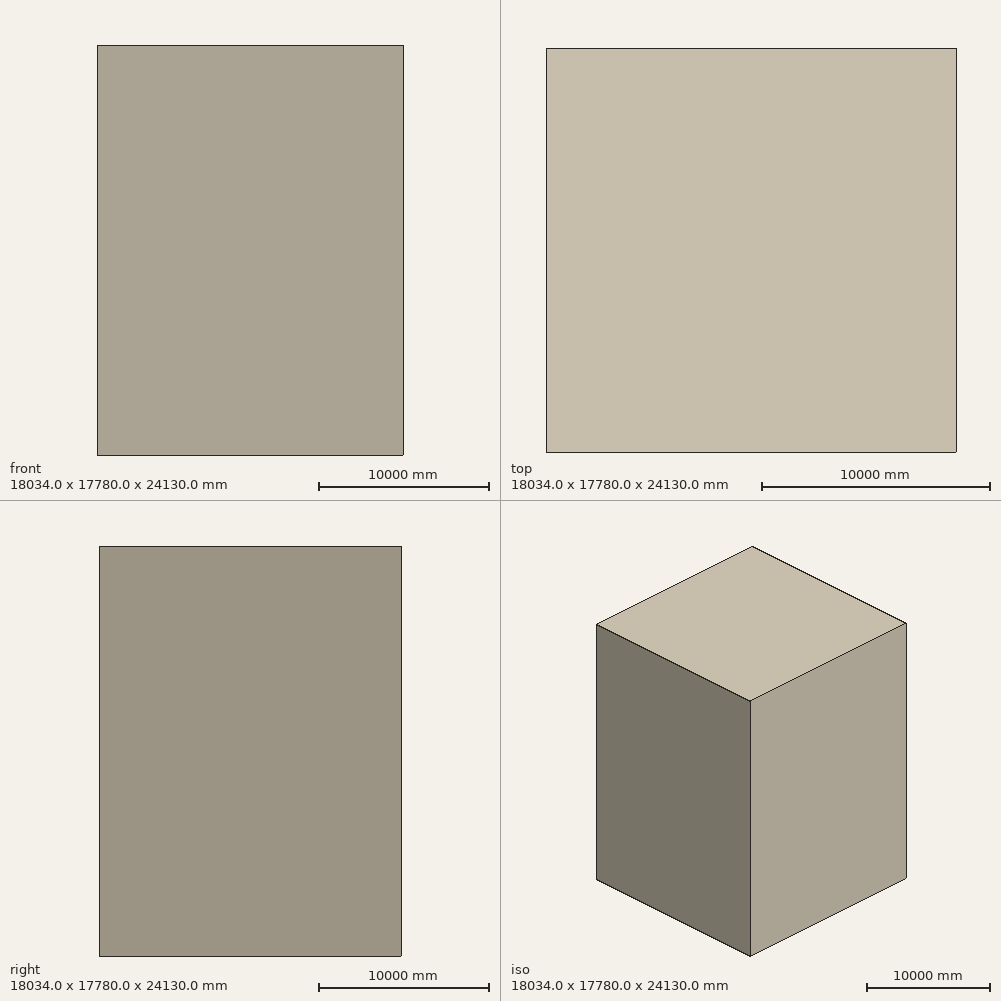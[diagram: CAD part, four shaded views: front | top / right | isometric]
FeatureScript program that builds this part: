
annotation { "Feature Type Name" : "Feature", "Feature Type Description" : "" }
export const myFeature = defineFeature(function(context is Context, id is Id, definition is map)
    precondition{}
    {
        {
            var Q0;
            Q0=qCreatedBy(makeId("Front.planeOp"),FACE);
            var sketch = newSketch(context, id + "F0", { "sketchPlane" : qUnion([Q0])});
            skLineSegment(sketch, "E0.bottom", {"start": v(0, 0) * mm, "end": v(18034, 0) * mm});
            skLineSegment(sketch, "E0.top", {"start": v(0, 24130) * mm, "end": v(18034, 24130) * mm});
            skLineSegment(sketch, "E0.left", {"start": v(0, 0) * mm, "end": v(0, 24130) * mm});
            skLineSegment(sketch, "E0.right", {"start": v(18034, 0) * mm, "end": v(18034, 24130) * mm});
            skSolve(sketch);
        }
        {
            var Q0;
            Q0=makeQuery(id+"F0.imprint","IMPRINT",FACE,{"disambiguationData":[TD([[makeQuery(id+"F0.imprint","IMPRINT",EDGE,{"derivedFrom":sQuery(id+"F0.wireOp",EDGE,"E0.bottom")}),1.0]])]});
            extrude(context, id + "F1", {"entities" : qUnion([Q0]), "oppositeDirection" : true, "depth" : 17780 * mm, "offsetDistance" : 25.4 * mm});
        }
        {
            var Q0;
            Q0=makeQuery(id+"F1.opExtrude","CAP_FACE",FACE,{"disambiguationData":[OSD([sQuery(id+"F0.wireOp",EDGE,"E0.bottom"),sQuery(id+"F0.wireOp",EDGE,"E0.top"),sQuery(id+"F0.wireOp",EDGE,"E0.left"),sQuery(id+"F0.wireOp",EDGE,"E0.right")])],"isStart":false});
            var sketch = newSketch(context, id + "F2", { "sketchPlane" : qUnion([Q0])});
            skLineSegment(sketch, "E1.bottom", {"start": v(-152.4, 152.4) * mm, "end": v(-17881.6, 152.4) * mm});
            skLineSegment(sketch, "E1.top", {"start": v(-152.4, 23977.6) * mm, "end": v(-17881.6, 23977.6) * mm});
            skLineSegment(sketch, "E1.left", {"start": v(-152.4, 152.4) * mm, "end": v(-152.4, 23977.6) * mm});
            skLineSegment(sketch, "E1.right", {"start": v(-17881.6, 152.4) * mm, "end": v(-17881.6, 23977.6) * mm});
            skSolve(sketch);
        }
        {
            var Q0;
            Q0 = qSketchRegion(id + "F2", true);
            extrude(context, id + "F3", {"entities" : qUnion([Q0]), "operationType" : NewBodyOperationType.REMOVE, "oppositeDirection" : true, "depth" : 17627.6 * mm, "offsetDistance" : 25.4 * mm});
        }
        {
            var Q0;
            Q0=makeQuery(id+"F1.opExtrude","SWEPT_FACE",FACE,{"disambiguationData":[OSD([sQuery(id+"F0.wireOp",EDGE,"E0.right")])]});
            var sketch = newSketch(context, id + "F4", { "sketchPlane" : qUnion([Q0])});
            skLineSegment(sketch, "E2.bottom", {"start": v(17780, 24130) * mm, "end": v(17780, 24130) * mm});
            skLineSegment(sketch, "E2.top", {"start": v(17780, 0) * mm, "end": v(17780, 0) * mm});
            skLineSegment(sketch, "E2.left", {"start": v(17780, 24130) * mm, "end": v(17780, 0) * mm});
            skLineSegment(sketch, "E2.right", {"start": v(17780, 24130) * mm, "end": v(17780, 0) * mm});
            skLineSegment(sketch, "E3.left", {"start": v(17780, 0) * mm, "end": v(17780, 24130) * mm});
            skLineSegment(sketch, "E3.right", {"start": v(17780, 0) * mm, "end": v(17780, 24130) * mm});
            skLineSegment(sketch, "E4.bottom", {"start": v(17780, 0) * mm, "end": v(17627.6, 0) * mm});
            skLineSegment(sketch, "E4.top", {"start": v(17780, 24130) * mm, "end": v(17627.6, 24130) * mm});
            skLineSegment(sketch, "E4.right", {"start": v(17627.6, 0) * mm, "end": v(17627.6, 24130) * mm});
            skSolve(sketch);
        }
        {
            var Q0;
            Q0 = qSketchRegion(id + "F4", true);
            extrude(context, id + "F5", {"entities" : qUnion([Q0]), "operationType" : NewBodyOperationType.ADD, "oppositeDirection" : true, "depth" : 18034 * mm, "offsetDistance" : 25.4 * mm});
        }
        {
            var Q0;
            Q0=makeQuery(id+"F5.boolean.opBoolean","MERGE",FACE,{"derivedFrom":[makeQuery(id+"F1.opExtrude","CAP_FACE",FACE,{"disambiguationData":[OSD([sQuery(id+"F0.wireOp",EDGE,"E0.bottom"),sQuery(id+"F0.wireOp",EDGE,"E0.top"),sQuery(id+"F0.wireOp",EDGE,"E0.left"),sQuery(id+"F0.wireOp",EDGE,"E0.right")])],"isStart":false}),makeQuery(id+"F5.opExtrude","SWEPT_FACE",FACE,{"disambiguationData":[OSD([sQuery(id+"F4.wireOp",EDGE,"E3.left")])]})]});
            var sketch = newSketch(context, id + "F6", { "sketchPlane" : qUnion([Q0])});
            skLineSegment(sketch, "E5.bottom", {"start": v(-16764, 21590) * mm, "end": v(-1270, 21590) * mm});
            skLineSegment(sketch, "E5.top", {"start": v(-16764, 2540) * mm, "end": v(-1270, 2540) * mm});
            skLineSegment(sketch, "E5.left", {"start": v(-16764, 21590) * mm, "end": v(-16764, 2540) * mm});
            skLineSegment(sketch, "E5.right", {"start": v(-1270, 21590) * mm, "end": v(-1270, 2540) * mm});
            skSolve(sketch);
        }
        {
            var Q0;
            Q0 = qSketchRegion(id + "F6", true);
            extrude(context, id + "F7", {"entities" : qUnion([Q0]), "operationType" : NewBodyOperationType.REMOVE, "oppositeDirection" : true, "depth" : 203.2 * mm, "offsetDistance" : 25.4 * mm});
        }
        {
            var Q0;
            Q0=makeQuery(id+"F1.opExtrude","SWEPT_FACE",FACE,{"disambiguationData":[OSD([sQuery(id+"F0.wireOp",EDGE,"E0.bottom")])]});
            var sketch = newSketch(context, id + "F8", { "sketchPlane" : qUnion([Q0])});
            skLineSegment(sketch, "E6", {"start": v(2514.6, -4775.2) * mm, "end": v(5054.6, -4775.2) * mm});
            skLineSegment(sketch, "E7", {"start": v(5054.6, -4775.2) * mm, "end": v(5054.6, -4927.6) * mm});
            skLineSegment(sketch, "E8", {"start": v(5054.6, -4927.6) * mm, "end": v(2667, -4927.6) * mm});
            skLineSegment(sketch, "E9", {"start": v(2667, -4927.6) * mm, "end": v(2667, -7315.2) * mm});
            skLineSegment(sketch, "E10", {"start": v(2667, -7315.2) * mm, "end": v(2514.6, -7315.2) * mm});
            skLineSegment(sketch, "E11", {"start": v(2514.6, -4775.2) * mm, "end": v(2514.6, -7315.2) * mm});
            skPoint(sketch, "E12.endSnap0", {"position": v(9017, -17780) * mm});
            skLineSegment(sketch, "E13", {"start": v(9017, 0) * mm, "end": v(9017, -17780) * mm});
            skLineSegment(sketch, "E14.MirrorCS", {"start": v(15367, -7315.2) * mm, "end": v(15519.4, -7315.2) * mm});
            skLineSegment(sketch, "E15.MirrorCS", {"start": v(15367, -4927.6) * mm, "end": v(15367, -7315.2) * mm});
            skLineSegment(sketch, "E16.MirrorCS", {"start": v(12979.4, -4775.2) * mm, "end": v(12979.4, -4927.6) * mm});
            skLineSegment(sketch, "E17.MirrorCS", {"start": v(12979.4, -4927.6) * mm, "end": v(15367, -4927.6) * mm});
            skLineSegment(sketch, "E18.MirrorCS", {"start": v(15519.4, -4775.2) * mm, "end": v(15519.4, -7315.2) * mm});
            skLineSegment(sketch, "E19.MirrorCS", {"start": v(15519.4, -4775.2) * mm, "end": v(12979.4, -4775.2) * mm});
            skSolve(sketch);
        }
        {
            var Q0;
            Q0 = qSketchRegion(id + "F8", true);
            extrude(context, id + "F9", {"entities" : qUnion([Q0]), "operationType" : NewBodyOperationType.ADD, "oppositeDirection" : true, "depth" : 24130 * mm, "offsetDistance" : 25.4 * mm});
        }
    });
